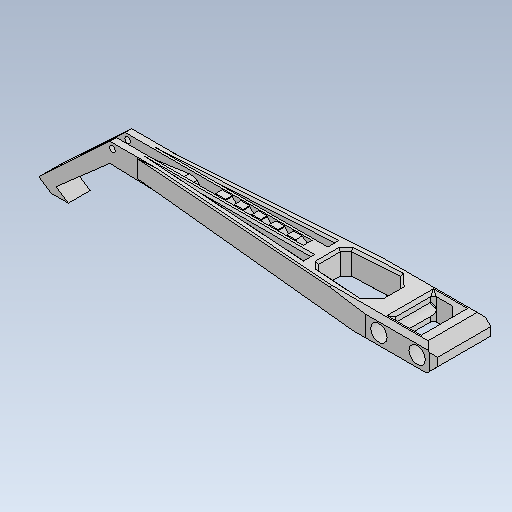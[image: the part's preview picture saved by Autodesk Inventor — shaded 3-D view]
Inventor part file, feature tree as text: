
AUTODESK INVENTOR PART (.ipt)
format: ipt  version: 2023 (Build 270158030, 158C)  size: 276,992 bytes
history: native  units: mm
features: other x4, chamfer x1
ambient origin geometry x8: Origin, YZ Plane, XZ Plane, XY Plane, X Axis, Y Axis, Z Axis, Center Point
bodies: Body1 (feature_tree)
feature tree (5):
  other  "V4.0-trebuchet-complete-parts.ipt"
  chamfer  "Chamfer1"  Distance=10.0mm
  other  "throw-arm-top::V4.0-trebuchet-complete-parts.ipt"
  other  "TaggingFeature1"
  other  "throw-arm-top"
